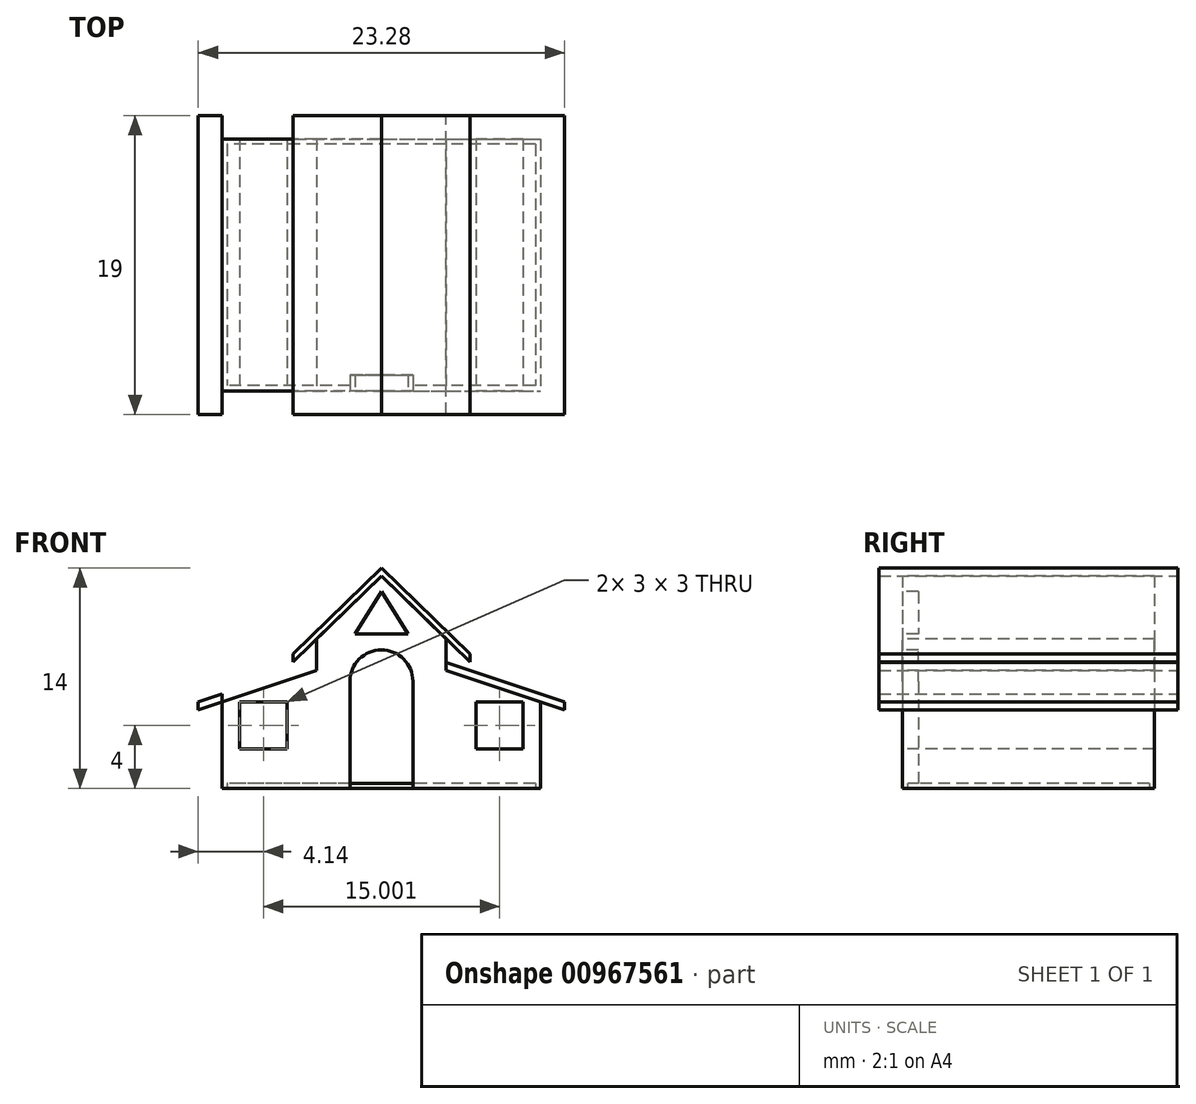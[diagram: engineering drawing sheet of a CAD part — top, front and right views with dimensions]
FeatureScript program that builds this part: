
annotation { "Feature Type Name" : "Feature", "Feature Type Description" : "" }
export const myFeature = defineFeature(function(context is Context, id is Id, definition is map)
    precondition{}
    {
        {
            var Q0;
            Q0=qCreatedBy(makeId("Front.planeOp"),FACE);
            var sketch = newSketch(context, id + "F0", { "sketchPlane" : qUnion([Q0])});
            skPoint(sketch, "E0.middle", {"position": v(0, 0) * mm});
            skLineSegment(sketch, "E1", {"start": v(0, -14.28) * mm, "end": v(0, 14.78) * mm, "construction": true});
            skLineSegment(sketch, "E2", {"start": v(-4.12, -4) * mm, "end": v(-4.12, 6) * mm});
            skPoint(sketch, "E3", {"position": v(0, 10) * mm});
            skLineSegment(sketch, "E4", {"start": v(0, 10) * mm, "end": v(-5.62, 4.54) * mm});
            skLineSegment(sketch, "E5", {"start": v(-4.12, 4) * mm, "end": v(-11.64, 1.5) * mm});
            skLineSegment(sketch, "E6", {"start": v(-10.12, 2) * mm, "end": v(-10.12, -4) * mm});
            skLineSegment(sketch, "E7", {"start": v(-10.12, -4) * mm, "end": v(0, -4) * mm});
            skArc(sketch, "E8", {"start": v(0, 4.8) * mm, "mid": v(-1.41, 4.21) * mm, "end": v(-2, 2.8) * mm});
            skLineSegment(sketch, "E9", {"start": v(-2, 2.8) * mm, "end": v(-2, -4) * mm});
            skPoint(sketch, "E10.middle", {"position": v(-7.5, 0) * mm});
            skLineSegment(sketch, "E11.bottom", {"start": v(-9, 1.5) * mm, "end": v(-6, 1.5) * mm});
            skLineSegment(sketch, "E11.top", {"start": v(-9, -1.5) * mm, "end": v(-6, -1.5) * mm});
            skLineSegment(sketch, "E11.left", {"start": v(-9, 1.5) * mm, "end": v(-9, -1.5) * mm});
            skLineSegment(sketch, "E11.right", {"start": v(-6, 1.5) * mm, "end": v(-6, -1.5) * mm});
            skLineSegment(sketch, "E12", {"start": v(0, 10) * mm, "end": v(0, 9.5) * mm});
            skLineSegment(sketch, "E13", {"start": v(0, 9.5) * mm, "end": v(-5.62, 4.04) * mm});
            skLineSegment(sketch, "E14", {"start": v(-5.62, 4.04) * mm, "end": v(-5.62, 4.54) * mm});
            skLineSegment(sketch, "E15", {"start": v(-4.12, 4) * mm, "end": v(-4.12, 3.5) * mm});
            skLineSegment(sketch, "E16", {"start": v(-4.12, 3.5) * mm, "end": v(-11.64, 1) * mm});
            skLineSegment(sketch, "E17", {"start": v(-11.64, 1) * mm, "end": v(-11.64, 1.5) * mm});
            skLineSegment(sketch, "E18.MirrorCS", {"start": v(5.62, 4.04) * mm, "end": v(5.62, 4.54) * mm});
            skLineSegment(sketch, "E19.MirrorCS", {"start": v(11.64, 1) * mm, "end": v(11.64, 1.5) * mm});
            skLineSegment(sketch, "E20.MirrorCS", {"start": v(4.12, 4) * mm, "end": v(4.12, 3.5) * mm});
            skPoint(sketch, "E21.MirrorP", {"position": v(7.5, 0) * mm});
            skLineSegment(sketch, "E22.MirrorCS", {"start": v(9, 1.5) * mm, "end": v(9, -1.5) * mm});
            skLineSegment(sketch, "E23.MirrorCS", {"start": v(0, 10) * mm, "end": v(5.62, 4.54) * mm});
            skLineSegment(sketch, "E24.MirrorCS", {"start": v(9, 1.5) * mm, "end": v(6, 1.5) * mm});
            skLineSegment(sketch, "E25.MirrorCS", {"start": v(10.12, 2) * mm, "end": v(10.12, -4) * mm});
            skLineSegment(sketch, "E26.MirrorCS", {"start": v(4.12, 4) * mm, "end": v(11.64, 1.5) * mm});
            skLineSegment(sketch, "E27.MirrorCS", {"start": v(6, 1.5) * mm, "end": v(6, -1.5) * mm});
            skLineSegment(sketch, "E28.MirrorCS", {"start": v(4.12, 3.5) * mm, "end": v(11.64, 1) * mm});
            skLineSegment(sketch, "E29.MirrorCS", {"start": v(2, 2.8) * mm, "end": v(2, -4) * mm});
            skLineSegment(sketch, "E30.MirrorCS", {"start": v(10.12, -4) * mm, "end": v(0, -4) * mm});
            skLineSegment(sketch, "E31.MirrorCS", {"start": v(9, -1.5) * mm, "end": v(6, -1.5) * mm});
            skLineSegment(sketch, "E32.MirrorCS", {"start": v(4.12, -4) * mm, "end": v(4.12, 6) * mm});
            skLineSegment(sketch, "E33.MirrorCS", {"start": v(0, 9.5) * mm, "end": v(5.62, 4.04) * mm});
            skArc(sketch, "E34.MirrorCS", {"start": v(0, 4.8) * mm, "mid": v(1.41, 4.21) * mm, "end": v(2, 2.8) * mm});
            skLineSegment(sketch, "E35", {"start": v(0, 8.5) * mm, "end": v(-1.68, 5.8) * mm});
            skLineSegment(sketch, "E36", {"start": v(-1.68, 5.8) * mm, "end": v(0, 5.8) * mm});
            skLineSegment(sketch, "E37.MirrorCS", {"start": v(0, 8.5) * mm, "end": v(1.68, 5.8) * mm});
            skLineSegment(sketch, "E38.MirrorCS", {"start": v(1.68, 5.8) * mm, "end": v(0, 5.8) * mm});
            skPoint(sketch, "E39", {"position": v(-10.12, 1.5) * mm});
            skSolve(sketch);
        }
        {
            var Q0;
            {var subQ0=sQuery(id+"F0.wireOp",EDGE,"E15");Q0=makeQuery(id+"F0.imprint","IMPRINT",FACE,{"disambiguationData":[TD([[makeQuery(id+"F0.imprint","IMPRINT",EDGE,{"derivedFrom":subQ0}),-1.0]])]});}
            var Q1;
            {var subQ5=sQuery(id+"F0.wireOp",EDGE,"E12");Q1=makeQuery(id+"F0.imprint","IMPRINT",FACE,{"disambiguationData":[TD([[makeQuery(id+"F0.imprint","IMPRINT",EDGE,{"derivedFrom":subQ5}),-1.0]])]});}
            var Q2;
            {var subQ5=sQuery(id+"F0.wireOp",EDGE,"E14");Q2=makeQuery(id+"F0.imprint","IMPRINT",FACE,{"disambiguationData":[TD([[makeQuery(id+"F0.imprint","IMPRINT",EDGE,{"derivedFrom":subQ5}),-1.0]])]});}
            var Q3;
            {var subQ0=sQuery(id+"F0.wireOp",EDGE,"E12");Q3=makeQuery(id+"F0.imprint","IMPRINT",FACE,{"disambiguationData":[TD([[makeQuery(id+"F0.imprint","IMPRINT",EDGE,{"derivedFrom":subQ0}),1.0]])]});}
            var Q4;
            {var subQ0=sQuery(id+"F0.wireOp",EDGE,"E18.MirrorCS");Q4=makeQuery(id+"F0.imprint","IMPRINT",FACE,{"disambiguationData":[TD([[makeQuery(id+"F0.imprint","IMPRINT",EDGE,{"derivedFrom":subQ0}),1.0]])]});}
            var Q5;
            {var subQ0=sQuery(id+"F0.wireOp",EDGE,"E26.MirrorCS");var subQ1=sQuery(id+"F0.wireOp",EDGE,"E25.MirrorCS");var subQ2=makeQuery(id+"F0.imprint","INTERSECT",VERTEX,{"derivedFrom":[subQ1,subQ0]});Q5=makeQuery(id+"F0.imprint","IMPRINT",FACE,{"disambiguationData":[TD([[makeQuery(id+"F0.imprint","IMPRINT",EDGE,{"disambiguationData":[TD([[subQ2,-1.0]])],"derivedFrom":subQ1}),-1.0]])]});}
            var Q6;
            {var subQ0=sQuery(id+"F0.wireOp",EDGE,"E19.MirrorCS");Q6=makeQuery(id+"F0.imprint","IMPRINT",FACE,{"disambiguationData":[TD([[makeQuery(id+"F0.imprint","IMPRINT",EDGE,{"derivedFrom":subQ0}),1.0]])]});}
            var Q7;
            {var subQ0=sQuery(id+"F0.wireOp",EDGE,"E17");Q7=makeQuery(id+"F0.imprint","IMPRINT",FACE,{"disambiguationData":[TD([[makeQuery(id+"F0.imprint","IMPRINT",EDGE,{"derivedFrom":subQ0}),-1.0]])]});}
            extrude(context, id + "F1", {"entities" : qUnion([Q0, Q1, Q2, Q3, Q4, Q5, Q6, Q7]), "depth" : 1.5 * mm, "offsetDistance" : 25 * mm, "hasSecondDirection" : true, "secondDirectionOppositeDirection" : true, "secondDirectionDepth" : 17.5 * mm});
        }
        {
            var Q0;
            Q0=makeQuery(id+"F0.imprint","IMPRINT",FACE,{"disambiguationData":[TD([[makeQuery(id+"F0.imprint","IMPRINT",EDGE,{"derivedFrom":sQuery(id+"F0.wireOp",EDGE,"E11.bottom")}),1.0]])]});
            var Q1;
            Q1=makeQuery(id+"F0.imprint","IMPRINT",FACE,{"disambiguationData":[TD([[makeQuery(id+"F0.imprint","IMPRINT",EDGE,{"derivedFrom":sQuery(id+"F0.wireOp",EDGE,"E11.bottom")}),-1.0]])]});
            var Q2;
            Q2=makeQuery(id+"F0.imprint","IMPRINT",FACE,{"disambiguationData":[TD([[makeQuery(id+"F0.imprint","IMPRINT",EDGE,{"derivedFrom":sQuery(id+"F0.wireOp",EDGE,"E8")}),-1.0]])]});
            var Q3;
            Q3=makeQuery(id+"F0.imprint","IMPRINT",FACE,{"disambiguationData":[TD([[makeQuery(id+"F0.imprint","IMPRINT",EDGE,{"derivedFrom":sQuery(id+"F0.wireOp",EDGE,"E8")}),1.0]])]});
            var Q4;
            Q4=makeQuery(id+"F0.imprint","IMPRINT",FACE,{"disambiguationData":[TD([[makeQuery(id+"F0.imprint","IMPRINT",EDGE,{"derivedFrom":sQuery(id+"F0.wireOp",EDGE,"E22.MirrorCS")}),1.0]])]});
            var Q5;
            Q5=makeQuery(id+"F0.imprint","IMPRINT",FACE,{"disambiguationData":[TD([[makeQuery(id+"F0.imprint","IMPRINT",EDGE,{"derivedFrom":sQuery(id+"F0.wireOp",EDGE,"E22.MirrorCS")}),-1.0]])]});
            var Q6;
            Q6=makeQuery(id+"F0.imprint","IMPRINT",FACE,{"disambiguationData":[TD([[makeQuery(id+"F0.imprint","IMPRINT",EDGE,{"derivedFrom":sQuery(id+"F0.wireOp",EDGE,"E35")}),1.0]])]});
            extrude(context, id + "F2", {"entities" : qUnion([Q0, Q1, Q2, Q3, Q4, Q5, Q6]), "oppositeDirection" : true, "depth" : 16 * mm, "offsetDistance" : 25 * mm});
        }
        {
            var Q0;
            Q0=makeQuery(id+"F0.imprint","IMPRINT",FACE,{"disambiguationData":[TD([[makeQuery(id+"F0.imprint","IMPRINT",EDGE,{"derivedFrom":sQuery(id+"F0.wireOp",EDGE,"E8")}),1.0]])]});
            var Q1;
            Q1=makeQuery(id+"F0.imprint","IMPRINT",FACE,{"disambiguationData":[TD([[makeQuery(id+"F0.imprint","IMPRINT",EDGE,{"derivedFrom":sQuery(id+"F0.wireOp",EDGE,"E11.bottom")}),-1.0]])]});
            var Q2;
            Q2=makeQuery(id+"F0.imprint","IMPRINT",FACE,{"disambiguationData":[TD([[makeQuery(id+"F0.imprint","IMPRINT",EDGE,{"derivedFrom":sQuery(id+"F0.wireOp",EDGE,"E22.MirrorCS")}),-1.0]])]});
            var Q3;
            Q3=makeQuery(id+"F0.imprint","IMPRINT",FACE,{"disambiguationData":[TD([[makeQuery(id+"F0.imprint","IMPRINT",EDGE,{"derivedFrom":sQuery(id+"F0.wireOp",EDGE,"E35")}),1.0]])]});
            extrude(context, id + "F3", {"entities" : qUnion([Q0, Q1, Q2, Q3]), "operationType" : NewBodyOperationType.REMOVE, "oppositeDirection" : true, "depth" : 1 * mm, "offsetDistance" : 25 * mm});
        }
        {
            var Q0;
            Q0=makeQuery(id+"F0.imprint","IMPRINT",FACE,{"disambiguationData":[TD([[makeQuery(id+"F0.imprint","IMPRINT",EDGE,{"derivedFrom":sQuery(id+"F0.wireOp",EDGE,"E11.bottom")}),-1.0]])]});
            var Q1;
            Q1=makeQuery(id+"F0.imprint","IMPRINT",FACE,{"disambiguationData":[TD([[makeQuery(id+"F0.imprint","IMPRINT",EDGE,{"derivedFrom":sQuery(id+"F0.wireOp",EDGE,"E22.MirrorCS")}),-1.0]])]});
            extrude(context, id + "F4", {"entities" : qUnion([Q0, Q1]), "operationType" : NewBodyOperationType.REMOVE, "oppositeDirection" : true, "depth" : 17 * mm, "offsetDistance" : 25 * mm});
        }
        {
            var Q0;
            Q0=makeQuery(id+"F2.opExtrude","SWEPT_FACE",FACE,{"disambiguationData":[OSD([sQuery(id+"F0.wireOp",EDGE,"E7"),sQuery(id+"F0.wireOp",EDGE,"E30.MirrorCS")])]});
            cPlane(context, id + "F5", {"entities" : qUnion([Q0]), "cplaneType" : CPlaneType.OFFSET, "offset" : 0 * mm, "width" : 150 * mm, "height" : 150 * mm});
        }
        {
            var Q0;
            Q0=qCreatedBy(id+"F5.planeOp",FACE);
            var sketch = newSketch(context, id + "F6", { "sketchPlane" : qUnion([Q0])});
            skPoint(sketch, "E40", {"position": v(-9.8, -0.33) * mm});
            skPoint(sketch, "E41", {"position": v(9.79, -15.67) * mm});
            skLineSegment(sketch, "E42.bottom", {"start": v(9.79, -15.67) * mm, "end": v(-9.8, -15.67) * mm});
            skLineSegment(sketch, "E42.top", {"start": v(9.79, -0.33) * mm, "end": v(-9.8, -0.33) * mm});
            skLineSegment(sketch, "E42.left", {"start": v(9.79, -15.67) * mm, "end": v(9.79, -0.33) * mm});
            skLineSegment(sketch, "E42.right", {"start": v(-9.8, -15.67) * mm, "end": v(-9.8, -0.33) * mm});
            skSolve(sketch);
        }
        {
            var Q0;
            Q0=makeQuery(id+"F6.imprint","IMPRINT",FACE,{"disambiguationData":[TD([[makeQuery(id+"F6.imprint","IMPRINT",EDGE,{"derivedFrom":sQuery(id+"F6.wireOp",EDGE,"E42.bottom")}),-1.0]])]});
            extrude(context, id + "F7", {"entities" : qUnion([Q0]), "operationType" : NewBodyOperationType.REMOVE, "oppositeDirection" : true, "depth" : .333 * mm, "offsetDistance" : 25 * mm});
        }
    });
